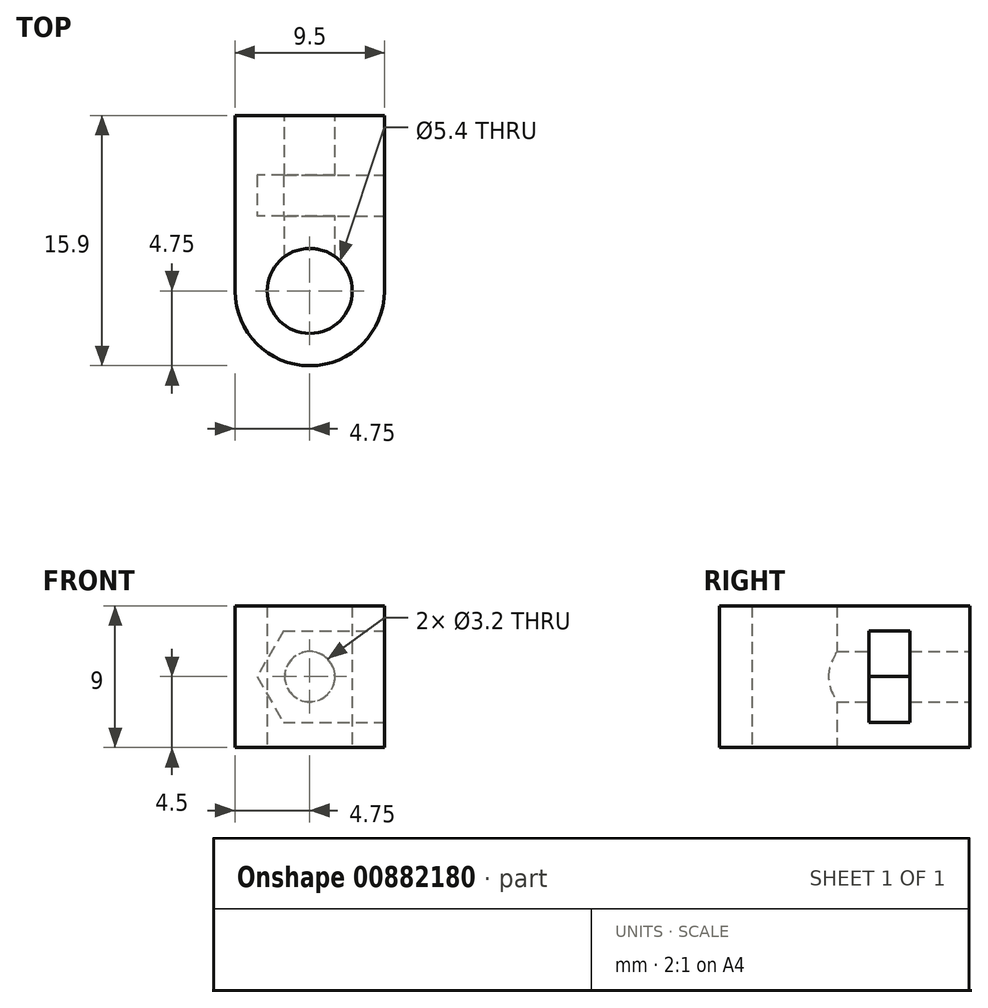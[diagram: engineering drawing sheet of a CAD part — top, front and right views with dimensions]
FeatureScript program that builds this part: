
annotation { "Feature Type Name" : "Feature", "Feature Type Description" : "" }
export const myFeature = defineFeature(function(context is Context, id is Id, definition is map)
    precondition{}
    {
        {
            var Q0;
            Q0=qCreatedBy(makeId("Top.planeOp"),FACE);
            var sketch = newSketch(context, id + "F0", { "sketchPlane" : qUnion([Q0])});
            skCircle(sketch, "E0", {"center": v(0, 0) * mm, "radius": 2.7 * mm});
            skCircle(sketch, "E1", {"center": v(0, 0) * mm, "radius": 4.75 * mm});
            skLineSegment(sketch, "E2", {"start": v(-4.75, 0) * mm, "end": v(-4.75, 4.75) * mm});
            skLineSegment(sketch, "E3", {"start": v(4.75, 0) * mm, "end": v(4.75, 4.75) * mm});
            skLineSegment(sketch, "E4", {"start": v(0, 4.75) * mm, "end": v(-4.75, 4.75) * mm});
            skLineSegment(sketch, "E5", {"start": v(-4.75, 4.75) * mm, "end": v(4.75, 4.75) * mm});
            skSolve(sketch);
        }
        {
            var Q0;
            {var subQ0=sQuery(id+"F0.wireOp",EDGE,"E3");Q0=makeQuery(id+"F0.imprint","IMPRINT",FACE,{"disambiguationData":[TD([[makeQuery(id+"F0.imprint","IMPRINT",EDGE,{"derivedFrom":subQ0}),1.0]])]});}
            var Q1;
            {var subQ0=sQuery(id+"F0.wireOp",EDGE,"E2");Q1=makeQuery(id+"F0.imprint","IMPRINT",FACE,{"disambiguationData":[TD([[makeQuery(id+"F0.imprint","IMPRINT",EDGE,{"derivedFrom":subQ0}),-1.0]])]});}
            var Q2;
            Q2=makeQuery(id+"F0.imprint","IMPRINT",FACE,{"disambiguationData":[TD([[makeQuery(id+"F0.imprint","IMPRINT",EDGE,{"derivedFrom":sQuery(id+"F0.wireOp",EDGE,"E0")}),-1.0]])]});
            extrude(context, id + "F1", {"entities" : qUnion([Q0, Q1, Q2]), "depth" : 9 * mm, "offsetDistance" : 25.4 * mm});
        }
        {
            var Q0;
            Q0=makeQuery(id+"F1.opExtrude","SWEPT_FACE",FACE,{"disambiguationData":[OSD([sQuery(id+"F0.wireOp",EDGE,"E5")])]});
            var sketch = newSketch(context, id + "F2", { "sketchPlane" : qUnion([Q0])});
            skLineSegment(sketch, "E6", {"start": v(-4.75, 9) * mm, "end": v(4.75, 0) * mm, "construction": true});
            skLineSegment(sketch, "E7", {"start": v(-4.75, 0) * mm, "end": v(4.75, 9) * mm, "construction": true});
            skCircle(sketch, "E8.cCircle", {"center": v(0, 4.5) * mm, "radius": 2.9 * mm, "construction": true});
            skLineSegment(sketch, "E8.0", {"start": v(-1.67, 7.4) * mm, "end": v(1.67, 7.4) * mm});
            skLineSegment(sketch, "E8.1", {"start": v(1.67, 7.4) * mm, "end": v(3.35, 4.5) * mm});
            skLineSegment(sketch, "E8.2", {"start": v(3.35, 4.5) * mm, "end": v(1.67, 1.6) * mm});
            skLineSegment(sketch, "E8.3", {"start": v(1.67, 1.6) * mm, "end": v(-1.67, 1.6) * mm});
            skLineSegment(sketch, "E8.4", {"start": v(-1.67, 1.6) * mm, "end": v(-3.35, 4.5) * mm});
            skLineSegment(sketch, "E8.5", {"start": v(-3.35, 4.5) * mm, "end": v(-1.67, 7.4) * mm});
            skPoint(sketch, "E8.0.midPoint", {"position": v(0, 7.4) * mm});
            skLineSegment(sketch, "E9", {"start": v(-1.67, 7.4) * mm, "end": v(-4.75, 7.4) * mm});
            skLineSegment(sketch, "E10", {"start": v(1.67, 1.6) * mm, "end": v(-4.75, 1.6) * mm});
            skSolve(sketch);
        }
        {
            var Q0;
            Q0=makeQuery(id+"F2.imprint","IMPRINT",FACE,{"disambiguationData":[TD([[makeQuery(id+"F2.imprint","IMPRINT",EDGE,{"derivedFrom":sQuery(id+"F2.wireOp",EDGE,"E8.0")}),1.0]])]});
            extrude(context, id + "F3", {"entities" : qUnion([Q0]), "operationType" : NewBodyOperationType.ADD, "depth" : 2.6 * mm, "offsetDistance" : 25.4 * mm});
        }
        {
            var Q0;
            Q0=makeQuery(id+"F3.opExtrude","CAP_FACE",FACE,{"disambiguationData":[OSD([sQuery(id+"F0.wireOp",EDGE,"E2"),sQuery(id+"F0.wireOp",EDGE,"E3"),sQuery(id+"F0.wireOp",EDGE,"E5"),sQuery(id+"F2.wireOp",EDGE,"E8.0"),sQuery(id+"F2.wireOp",EDGE,"E8.1"),sQuery(id+"F2.wireOp",EDGE,"E8.2"),sQuery(id+"F2.wireOp",EDGE,"E9"),sQuery(id+"F2.wireOp",EDGE,"E10")])],"isStart":false});
            var sketch = newSketch(context, id + "F4", { "sketchPlane" : qUnion([Q0])});
            skLineSegment(sketch, "E11.bottom", {"start": v(-4.75, 9) * mm, "end": v(4.75, 9) * mm});
            skLineSegment(sketch, "E11.top", {"start": v(-4.75, 0) * mm, "end": v(4.75, 0) * mm});
            skLineSegment(sketch, "E11.left", {"start": v(-4.75, 9) * mm, "end": v(-4.75, 0) * mm});
            skLineSegment(sketch, "E11.right", {"start": v(4.75, 9) * mm, "end": v(4.75, 0) * mm});
            skSolve(sketch);
        }
        {
            var Q0;
            Q0=qSketchRegion(id+"F4",true);
            extrude(context, id + "F5", {"entities" : qUnion([Q0]), "operationType" : NewBodyOperationType.ADD, "depth" : 3.8 * mm, "offsetDistance" : 25.4 * mm});
        }
        {
            var Q0;
            Q0=makeQuery(id+"F5.opExtrude","CAP_FACE",FACE,{"disambiguationData":[OSD([sQuery(id+"F4.wireOp",EDGE,"E11.bottom"),sQuery(id+"F4.wireOp",EDGE,"E11.top"),sQuery(id+"F4.wireOp",EDGE,"E11.left"),sQuery(id+"F4.wireOp",EDGE,"E11.right")])],"isStart":false});
            var sketch = newSketch(context, id + "F6", { "sketchPlane" : qUnion([Q0])});
            skLineSegment(sketch, "E12", {"start": v(-4.75, 0) * mm, "end": v(4.75, 9) * mm, "construction": true});
            skLineSegment(sketch, "E13", {"start": v(-4.75, 9) * mm, "end": v(4.75, 0) * mm, "construction": true});
            skCircle(sketch, "E14", {"center": v(0, 4.5) * mm, "radius": 1.6 * mm});
            skSolve(sketch);
        }
        {
            var Q0;
            Q0=makeQuery(id+"F6.imprint","IMPRINT",FACE,{"disambiguationData":[TD([[makeQuery(id+"F6.imprint","IMPRINT",EDGE,{"derivedFrom":sQuery(id+"F6.wireOp",EDGE,"E14")}),1.0]])]});
            var Q1;
            Q1=sQuery(id+"F6.wireOp",EDGE,"E14");
            extrude(context, id + "F7", {"entities" : qUnion([Q0]), "operationType" : NewBodyOperationType.REMOVE, "surfaceEntities" : qUnion([Q1]), "oppositeDirection" : true, "depth" : 9 * mm, "offsetDistance" : 25.4 * mm});
        }
    });
